# Revit family: Balustrade1
name_source: partatom
category: Generic Models
units: mm (PartAtom-declared; Revit-internal decimal feet)

## family parameters
Always vertical = Yes
Can host rebar = No
Cut with Voids When Loaded = No
Maintain Annotation Orientation = No
Part Type = Normal
Room Calculation Point = No
Round Connector Dimension = Use Diameter
Shared = No
Work Plane-Based = No

## types (1)
- Balustrade1
    Angle of Inclination = 35.00°
    Balustrade Extension Lower Horizontal = 1405 mm
    Balustrade Extension Upper Horizontal = 1595 mm
    Balustrade Extension above Newel = 150 mm
    Balustrade Glass thickness = 4 mm  [stored 0.0131234 ft]
    Balustrade Width = 100 mm  [stored 0.328084 ft]
    Default Elevation = 0 mm  [stored 0 ft]
    Handrail Inner Radius = 550 mm
    Handrail Lower Inner Radius = 850 mm  [stored 2.78871 ft]
    Handrail Lower Radius = 800 mm  [stored 2.62467 ft]
    Handrail Thickness = 50 mm  [stored 0.164042 ft]
    Handrail Upper Inner Radius = 750 mm  [stored 2.46063 ft]
    Handrail Upper Radius = 800 mm  [stored 2.62467 ft]
    Handrail Vertical Height = 1350 mm  [stored 4.42913 ft]
    Handrail Width = 20 mm  [stored 0.0656168 ft]
    Lower Handrail Horizontal = 940 mm
    Lower Horizontal Distance = 1500 mm  [stored 4.92126 ft]
    Lower Radius of Curvature = 800 mm  [stored 2.62467 ft]
    Newel Entry FFL = 150 mm
    Newel Radius = 600 mm
    Newel Upper Horizontal = 1547 mm
    Rise = 6000 mm  [stored 19.685 ft]
    Transition Length = 8569 mm
    Upper Balustrade Horizontal = 1547 mm
    Upper Handrail Horizontal = 1500 mm  [stored 4.92126 ft]
    Upper Horizontal Distance = 1500 mm  [stored 4.92126 ft]
    Upper Radius of Curvature = 800 mm  [stored 2.62467 ft]

note: [stored X ft] marks values corroborated as IEEE doubles in the binary element streams (Revit-internal decimal feet)

## geometry (parser evidence)
native form markers: Sweep x2
no freeform markers — native parametric forms only
